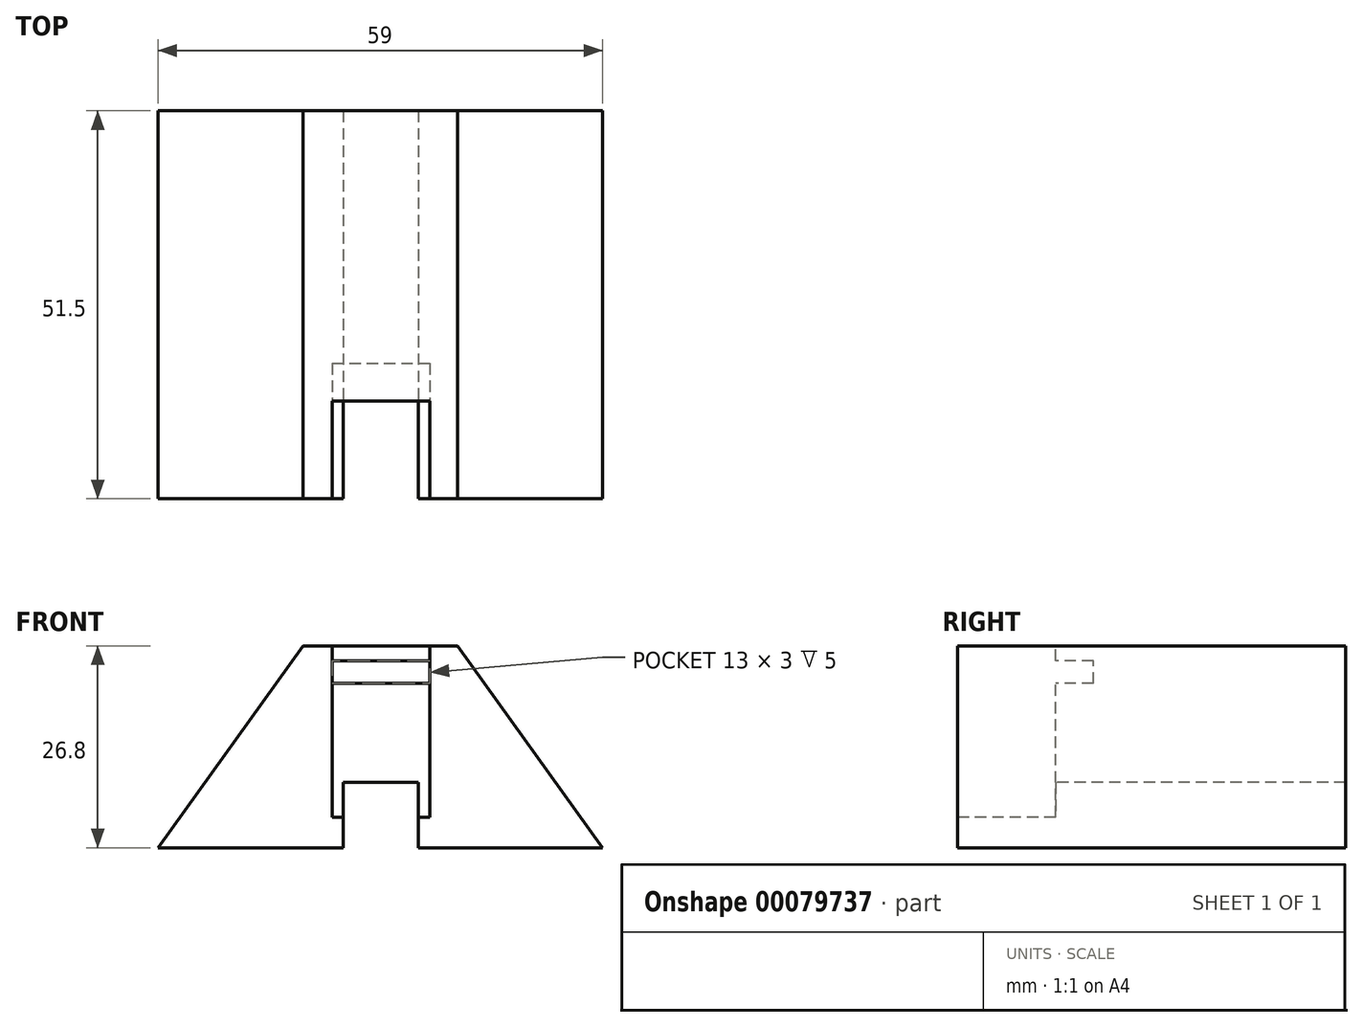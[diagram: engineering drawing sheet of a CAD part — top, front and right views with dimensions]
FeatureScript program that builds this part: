
annotation { "Feature Type Name" : "Feature", "Feature Type Description" : "" }
export const myFeature = defineFeature(function(context is Context, id is Id, definition is map)
    precondition{}
    {
        {
            var Q0;
            Q0=qCreatedBy(makeId("Top.planeOp"),FACE);
            var sketch = newSketch(context, id + "F0", { "sketchPlane" : qUnion([Q0])});
            skLineSegment(sketch, "E0.bottom", {"start": v(-29.5, -25.75) * mm, "end": v(29.5, -25.75) * mm});
            skLineSegment(sketch, "E0.top", {"start": v(-29.5, 25.75) * mm, "end": v(29.5, 25.75) * mm});
            skLineSegment(sketch, "E0.left", {"start": v(-29.5, -25.75) * mm, "end": v(-29.5, 25.75) * mm});
            skLineSegment(sketch, "E0.right", {"start": v(29.5, -25.75) * mm, "end": v(29.5, 25.75) * mm});
            skPoint(sketch, "E0.middle", {"position": v(0, 0) * mm});
            skLineSegment(sketch, "E1", {"start": v(0, 25.75) * mm, "end": v(0, -25.75) * mm, "construction": true});
            skSolve(sketch);
        }
        {
            var Q0;
            Q0=makeQuery(id+"F0.imprint","IMPRINT",FACE,{"disambiguationData":[TD([[makeQuery(id+"F0.imprint","IMPRINT",EDGE,{"derivedFrom":sQuery(id+"F0.wireOp",EDGE,"E0.bottom")}),1.0]])]});
            extrude(context, id + "F1", {"entities" : qUnion([Q0]), "depth" : 26.8 * mm});
        }
        {
            var Q0;
            Q0=makeQuery(id+"F1.opExtrude","SWEPT_FACE",FACE,{"disambiguationData":[OSD([sQuery(id+"F0.wireOp",EDGE,"E0.bottom")])]});
            var sketch = newSketch(context, id + "F2", { "sketchPlane" : qUnion([Q0])});
            skLineSegment(sketch, "E2", {"start": v(-29.5, 0) * mm, "end": v(-10.24, 26.8) * mm});
            skLineSegment(sketch, "E3", {"start": v(-10.24, 26.8) * mm, "end": v(-29.5, 26.8) * mm});
            skLineSegment(sketch, "E4", {"start": v(-29.5, 26.8) * mm, "end": v(-29.5, 0) * mm});
            skLineSegment(sketch, "E5", {"start": v(29.5, 0) * mm, "end": v(10.24, 26.8) * mm});
            skLineSegment(sketch, "E6", {"start": v(10.24, 26.8) * mm, "end": v(29.5, 26.8) * mm});
            skLineSegment(sketch, "E7", {"start": v(29.5, 26.8) * mm, "end": v(29.5, 0) * mm});
            skSolve(sketch);
        }
        {
            var Q0;
            Q0=makeQuery(id+"F2.imprint","IMPRINT",FACE,{"disambiguationData":[TD([[makeQuery(id+"F2.imprint","IMPRINT",EDGE,{"derivedFrom":sQuery(id+"F2.wireOp",EDGE,"E5")}),-1.0]])]});
            var Q1;
            Q1=makeQuery(id+"F2.imprint","IMPRINT",FACE,{"disambiguationData":[TD([[makeQuery(id+"F2.imprint","IMPRINT",EDGE,{"derivedFrom":sQuery(id+"F2.wireOp",EDGE,"E2")}),1.0]])]});
            extrude(context, id + "F3", {"entities" : qUnion([Q0, Q1]), "operationType" : NewBodyOperationType.REMOVE, "endBound" : BoundingType.THROUGH_ALL, "oppositeDirection" : true, "depth" : 25.4 * mm});
        }
        {
            var Q0;
            Q0=makeQuery(id+"F1.opExtrude","CAP_FACE",FACE,{"disambiguationData":[OSD([sQuery(id+"F0.wireOp",EDGE,"E0.bottom"),sQuery(id+"F0.wireOp",EDGE,"E0.top"),sQuery(id+"F0.wireOp",EDGE,"E0.left"),sQuery(id+"F0.wireOp",EDGE,"E0.right")])],"isStart":false});
            var sketch = newSketch(context, id + "F4", { "sketchPlane" : qUnion([Q0])});
            skLineSegment(sketch, "E8.bottom", {"start": v(-6.4, -12.75) * mm, "end": v(6.6, -12.75) * mm});
            skLineSegment(sketch, "E8.top", {"start": v(-6.4, -25.75) * mm, "end": v(6.6, -25.75) * mm});
            skLineSegment(sketch, "E8.left", {"start": v(-6.4, -12.75) * mm, "end": v(-6.4, -25.75) * mm});
            skLineSegment(sketch, "E8.right", {"start": v(6.6, -12.75) * mm, "end": v(6.6, -25.75) * mm});
            skSolve(sketch);
        }
        {
            var Q0;
            Q0 = qSketchRegion(id + "F4", true);
            extrude(context, id + "F5", {"entities" : qUnion([Q0]), "operationType" : NewBodyOperationType.REMOVE, "oppositeDirection" : true, "depth" : 22.75 * mm});
        }
        {
            var Q0;
            Q0=makeQuery(id+"F5.boolean.opBoolean","COPY",FACE,{"derivedFrom":makeQuery(id+"F5.opExtrude","SWEPT_FACE",FACE,{"disambiguationData":[OSD([sQuery(id+"F4.wireOp",EDGE,"E8.bottom")])]})});
            var sketch = newSketch(context, id + "F6", { "sketchPlane" : qUnion([Q0])});
            skLineSegment(sketch, "E9.bottom", {"start": v(-6.4, 24.8) * mm, "end": v(6.6, 24.8) * mm});
            skLineSegment(sketch, "E9.top", {"start": v(-6.4, 21.8) * mm, "end": v(6.6, 21.8) * mm});
            skLineSegment(sketch, "E9.left", {"start": v(-6.4, 24.8) * mm, "end": v(-6.4, 21.8) * mm});
            skLineSegment(sketch, "E9.right", {"start": v(6.6, 24.8) * mm, "end": v(6.6, 21.8) * mm});
            skSolve(sketch);
        }
        {
            var Q0;
            Q0 = qSketchRegion(id + "F6", true);
            extrude(context, id + "F7", {"entities" : qUnion([Q0]), "operationType" : NewBodyOperationType.REMOVE, "oppositeDirection" : true, "depth" : 5 * mm});
        }
        {
            var Q0;
            Q0=makeQuery(id+"F1.opExtrude","SWEPT_FACE",FACE,{"disambiguationData":[OSD([sQuery(id+"F0.wireOp",EDGE,"E0.bottom")])]});
            var sketch = newSketch(context, id + "F8", { "sketchPlane" : qUnion([Q0])});
            skLineSegment(sketch, "E10", {"start": v(0, 26.8) * mm, "end": v(0, -4) * mm, "construction": true});
            skSolve(sketch);
        }
        {
            var Q0;
            {var subQ2=sQuery(id+"F0.wireOp",EDGE,"E0.bottom");Q0=makeQuery(id+"F8.imprint","IMPRINT",FACE,{"disambiguationData":[TD([[makeQuery(id+"F8.imprint","IMPRINT",EDGE,{"derivedFrom":makeQuery(id+"F1.opExtrude","CAP_EDGE",EDGE,{"disambiguationData":[OSD([subQ2])],"isStart":true})}),1.0]])]});}
            var sketch = newSketch(context, id + "F9", { "sketchPlane" : qUnion([Q0])});
            skLineSegment(sketch, "E11.bottom", {"start": v(-4.92, 8.67) * mm, "end": v(5.08, 8.67) * mm});
            skLineSegment(sketch, "E11.top", {"start": v(-4.92, 0) * mm, "end": v(5.08, 0) * mm});
            skLineSegment(sketch, "E11.left", {"start": v(-4.92, 8.67) * mm, "end": v(-4.92, 0) * mm});
            skLineSegment(sketch, "E11.right", {"start": v(5.08, 8.67) * mm, "end": v(5.08, 0) * mm});
            skSolve(sketch);
        }
        {
            var Q0;
            Q0 = qSketchRegion(id + "F9", true);
            extrude(context, id + "F10", {"entities" : qUnion([Q0]), "operationType" : NewBodyOperationType.REMOVE, "endBound" : BoundingType.THROUGH_ALL, "oppositeDirection" : true, "depth" : 25.4 * mm});
        }
    });
